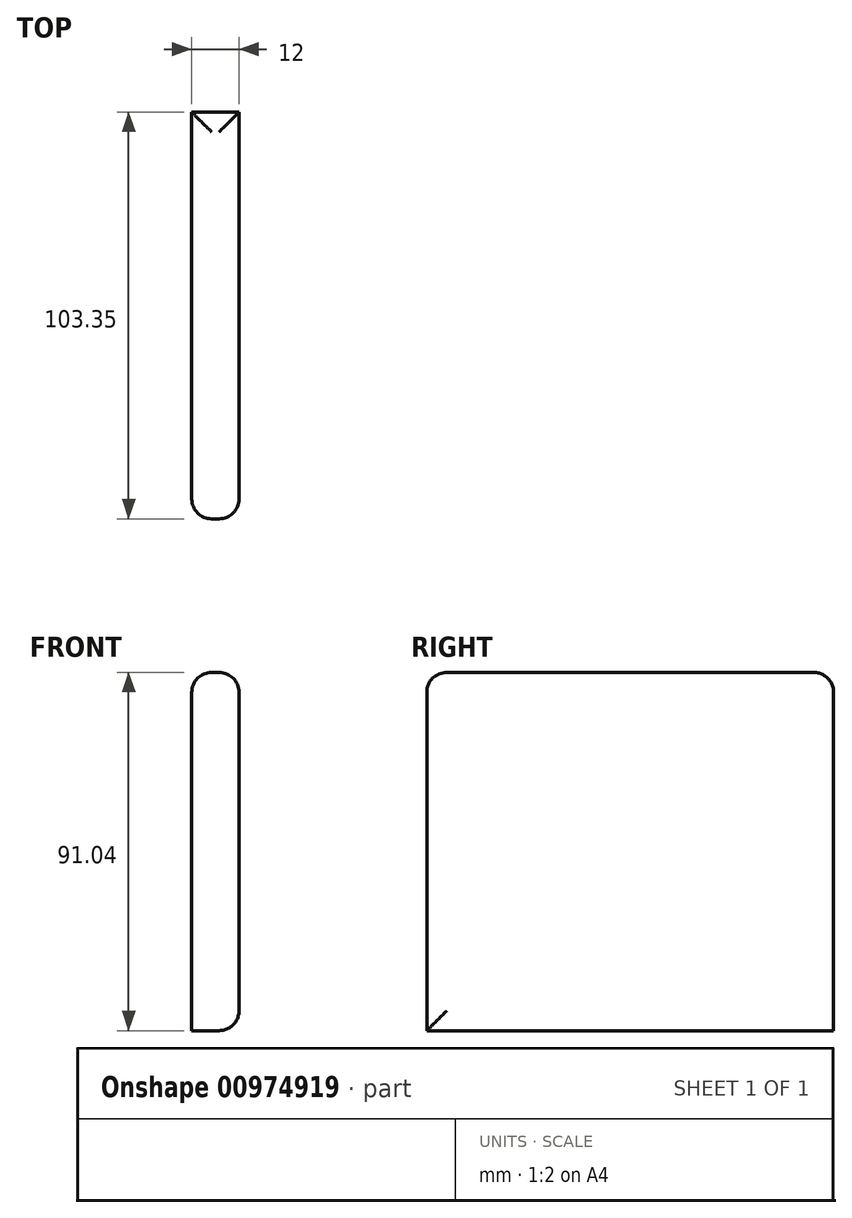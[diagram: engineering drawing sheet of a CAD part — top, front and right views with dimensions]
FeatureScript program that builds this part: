
annotation { "Feature Type Name" : "Feature", "Feature Type Description" : "" }
export const myFeature = defineFeature(function(context is Context, id is Id, definition is map)
    precondition{}
    {
        {
            var Q0;
            Q0=qCreatedBy(makeId("Right.planeOp"),FACE);
            var sketch = newSketch(context, id + "F0", { "sketchPlane" : qUnion([Q0])});
            skLineSegment(sketch, "E0.bottom", {"start": v(44.7, 45.75) * mm, "end": v(-58.64, 45.75) * mm});
            skLineSegment(sketch, "E0.top", {"start": v(44.7, -45.29) * mm, "end": v(-58.64, -45.29) * mm});
            skLineSegment(sketch, "E0.left", {"start": v(44.7, 45.75) * mm, "end": v(44.7, -45.29) * mm});
            skLineSegment(sketch, "E0.right", {"start": v(-58.64, 45.75) * mm, "end": v(-58.64, -45.29) * mm});
            skSolve(sketch);
        }
        {
            var Q0;
            Q0=makeQuery(id+"F0.imprint","IMPRINT",FACE,{"disambiguationData":[TD([[makeQuery(id+"F0.imprint","IMPRINT",EDGE,{"derivedFrom":sQuery(id+"F0.wireOp",EDGE,"E0.bottom")}),1.0]])]});
            extrude(context, id + "F1", {"entities" : qUnion([Q0]), "depth" : 12 * mm, "offsetDistance" : 25.4 * mm});
        }
        {
            var Q0;
            Q0=makeQuery(id+"F1.opExtrude","SWEPT_EDGE",EDGE,{"disambiguationData":[OSD([sQuery(id+"F0.wireOp",EDGE,"E0.bottom"),sQuery(id+"F0.wireOp",EDGE,"E0.right")])]});
            var Q1;
            Q1=makeQuery(id+"F1.opExtrude","CAP_EDGE",EDGE,{"disambiguationData":[OSD([sQuery(id+"F0.wireOp",EDGE,"E0.bottom")])],"isStart":false});
            var Q2;
            Q2=makeQuery(id+"F1.opExtrude","CAP_EDGE",EDGE,{"disambiguationData":[OSD([sQuery(id+"F0.wireOp",EDGE,"E0.bottom")])],"isStart":true});
            var Q3;
            Q3=makeQuery(id+"F1.opExtrude","SWEPT_EDGE",EDGE,{"disambiguationData":[OSD([sQuery(id+"F0.wireOp",EDGE,"E0.bottom"),sQuery(id+"F0.wireOp",EDGE,"E0.left")])]});
            var Q4;
            Q4=makeQuery(id+"F1.opExtrude","CAP_EDGE",EDGE,{"disambiguationData":[OSD([sQuery(id+"F0.wireOp",EDGE,"E0.right")])],"isStart":false});
            var Q5;
            Q5=makeQuery(id+"F1.opExtrude","CAP_EDGE",EDGE,{"disambiguationData":[OSD([sQuery(id+"F0.wireOp",EDGE,"E0.right")])],"isStart":true});
            var Q6;
            Q6=makeQuery(id+"F1.opExtrude","CAP_EDGE",EDGE,{"disambiguationData":[OSD([sQuery(id+"F0.wireOp",EDGE,"E0.top")])],"isStart":false});
            fillet(context, id + "F2", {"entities" : qUnion([Q0, Q1, Q2, Q3, Q4, Q5, Q6]), "radius" : 5.08 * mm, "tangentPropagation" : true, "allowEdgeOverflow" : false});
        }
    });
